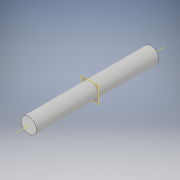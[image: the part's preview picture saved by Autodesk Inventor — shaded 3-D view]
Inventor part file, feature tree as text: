
AUTODESK INVENTOR PART (.ipt)
format: ipt  version: 2019.1 (Build 231200000, 200)  size: 96,256 bytes
history: native  units: in
note: dims shown in document units (in); Inventor stores cm internally (conversion verified against a paired STEP export)
features: extrude x1, sketch x1
ambient origin geometry x8: Origin, YZ Plane, XZ Plane, XY Plane, X Axis, Y Axis, Z Axis, Center Point
bodies: Solid1 (feature_tree)
feature tree (2):
  extrude  "Extrusion1"  Depth=2.0in TaperAngle=0.0deg
  sketch  "Sketch1"  dims[d0=0.25in d1=2.0in d2=0.0in]
